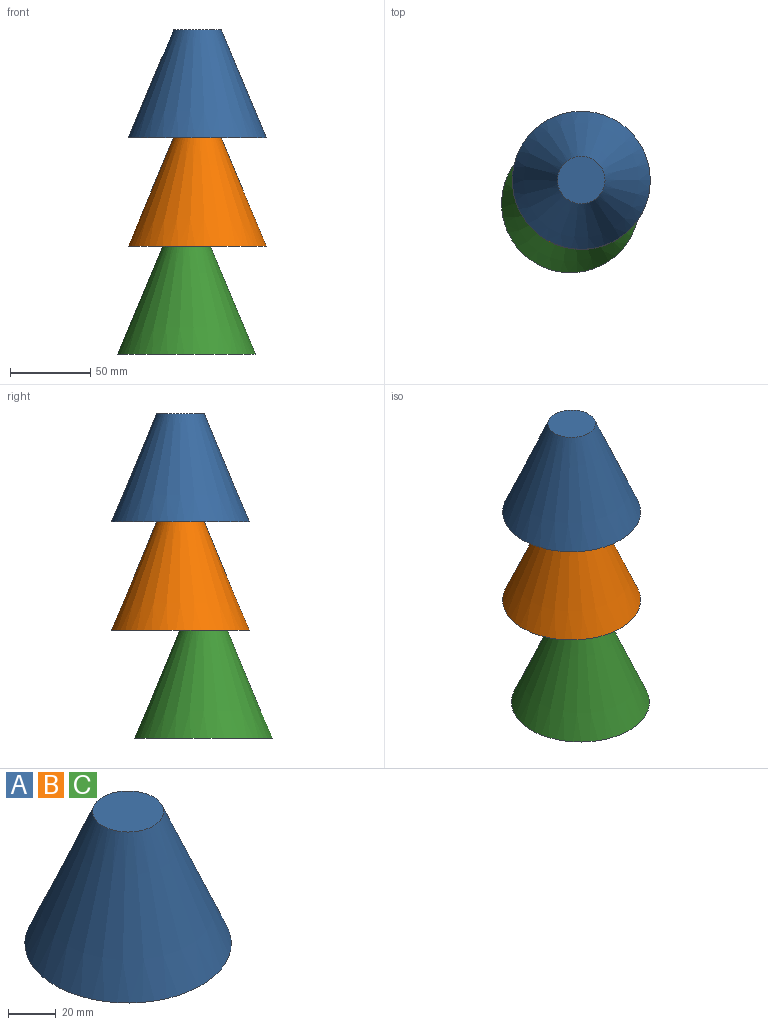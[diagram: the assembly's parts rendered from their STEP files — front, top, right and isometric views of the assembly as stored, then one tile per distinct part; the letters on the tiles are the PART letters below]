
ASSEMBLY  parts=3 mates=2
PART A: 3 faces, bbox 86.2x86.2x67.4 mm
  f0: plane 29.69x29.69mm, normal (0,0,1), area 692.1mm2, adj f2
  f1: plane 86.15x86.15mm, normal (0,0,-1), area 5829.5mm2, adj f2
  f2: cone r=43.08mm half-angle=22.7deg, axis (0,0,-1), area 13302.2mm2, adj f0,f1
PART B: same geometry as A
PART C: same geometry as A
PLACE A t=(-19.88,29.86,67.67)mm
PLACE B t=(-19.88,29.86,0.24)mm
PLACE C t=(-26.58,15.44,-67.19)mm
MATE planar A.f2 <-> B.f2  axis (0,0,-1) through (-19.88,29.86,67.67)mm
MATE planar B.f2 <-> C.f2  axis (0,0,-1) through (-19.88,29.86,0.24)mm
